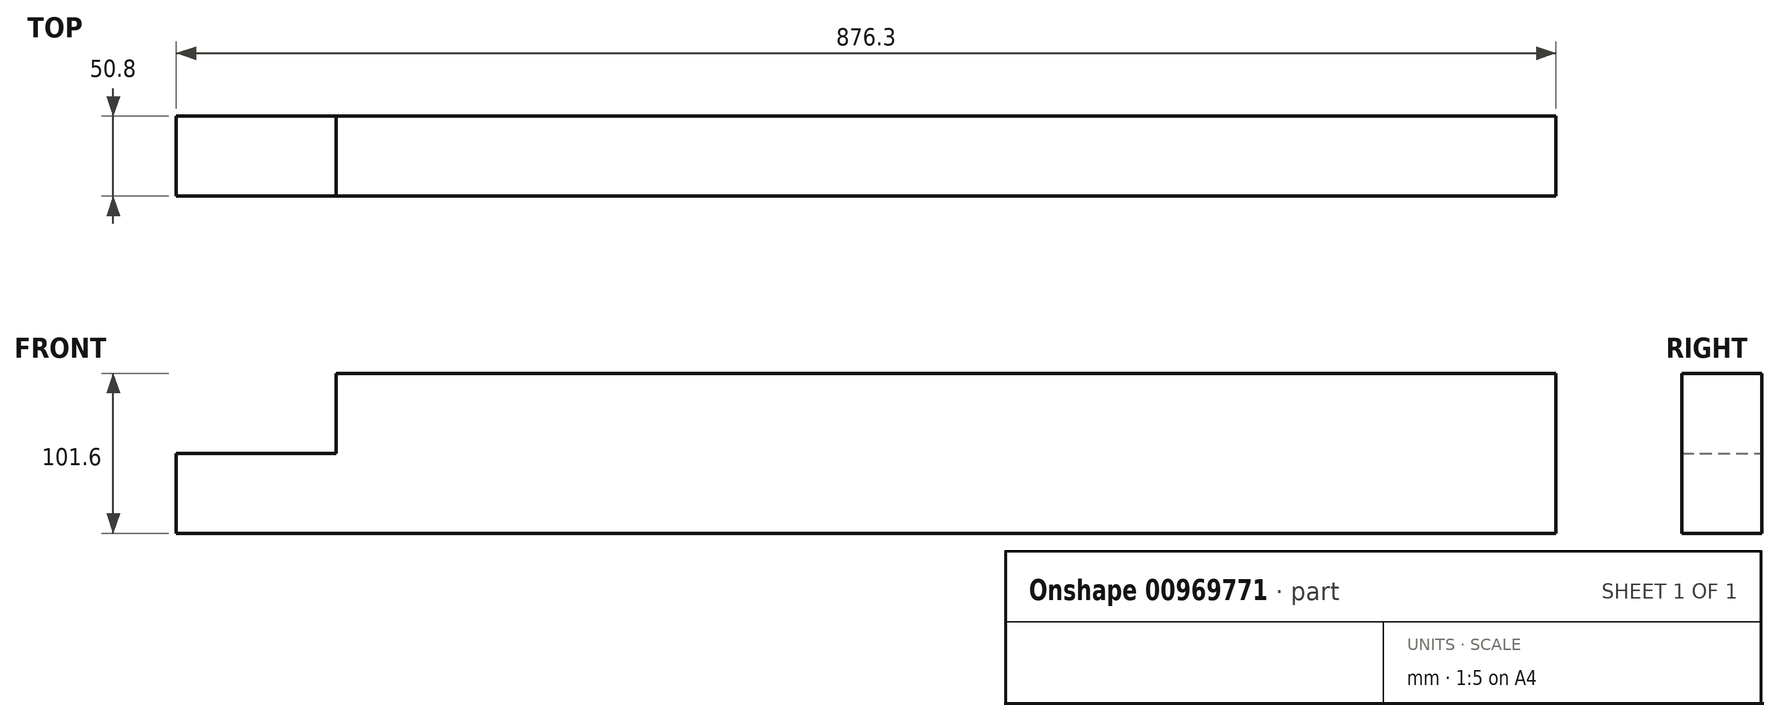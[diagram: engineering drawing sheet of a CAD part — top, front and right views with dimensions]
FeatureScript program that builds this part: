
annotation { "Feature Type Name" : "Feature", "Feature Type Description" : "" }
export const myFeature = defineFeature(function(context is Context, id is Id, definition is map)
    precondition{}
    {
        {
            var Q0;
            Q0=qCreatedBy(makeId("Front.planeOp"),FACE);
            var sketch = newSketch(context, id + "F0", { "sketchPlane" : qUnion([Q0])});
            skLineSegment(sketch, "E0.bottom", {"start": v(-336.55, 50.8) * mm, "end": v(438.15, 50.8) * mm});
            skLineSegment(sketch, "E0.top", {"start": v(-438.15, -50.8) * mm, "end": v(438.15, -50.8) * mm});
            skLineSegment(sketch, "E0.left", {"start": v(-438.15, 0) * mm, "end": v(-438.15, -50.8) * mm});
            skLineSegment(sketch, "E0.right", {"start": v(438.15, 50.8) * mm, "end": v(438.15, -50.8) * mm});
            skPoint(sketch, "E0.middle", {"position": v(0, 0) * mm});
            skLineSegment(sketch, "E1", {"start": v(-438.15, 0) * mm, "end": v(-336.55, 0) * mm});
            skLineSegment(sketch, "E2", {"start": v(-336.55, 0) * mm, "end": v(-336.55, 50.8) * mm});
            skPoint(sketch, "E3.orphan", {"position": v(-438.15, 50.8) * mm});
            skSolve(sketch);
        }
        {
            var Q0;
            Q0 = qSketchRegion(id + "F0", true);
            extrude(context, id + "F1", {"entities" : qUnion([Q0]), "depth" : 50.8 * mm, "offsetDistance" : 25.4 * mm});
        }
    });
